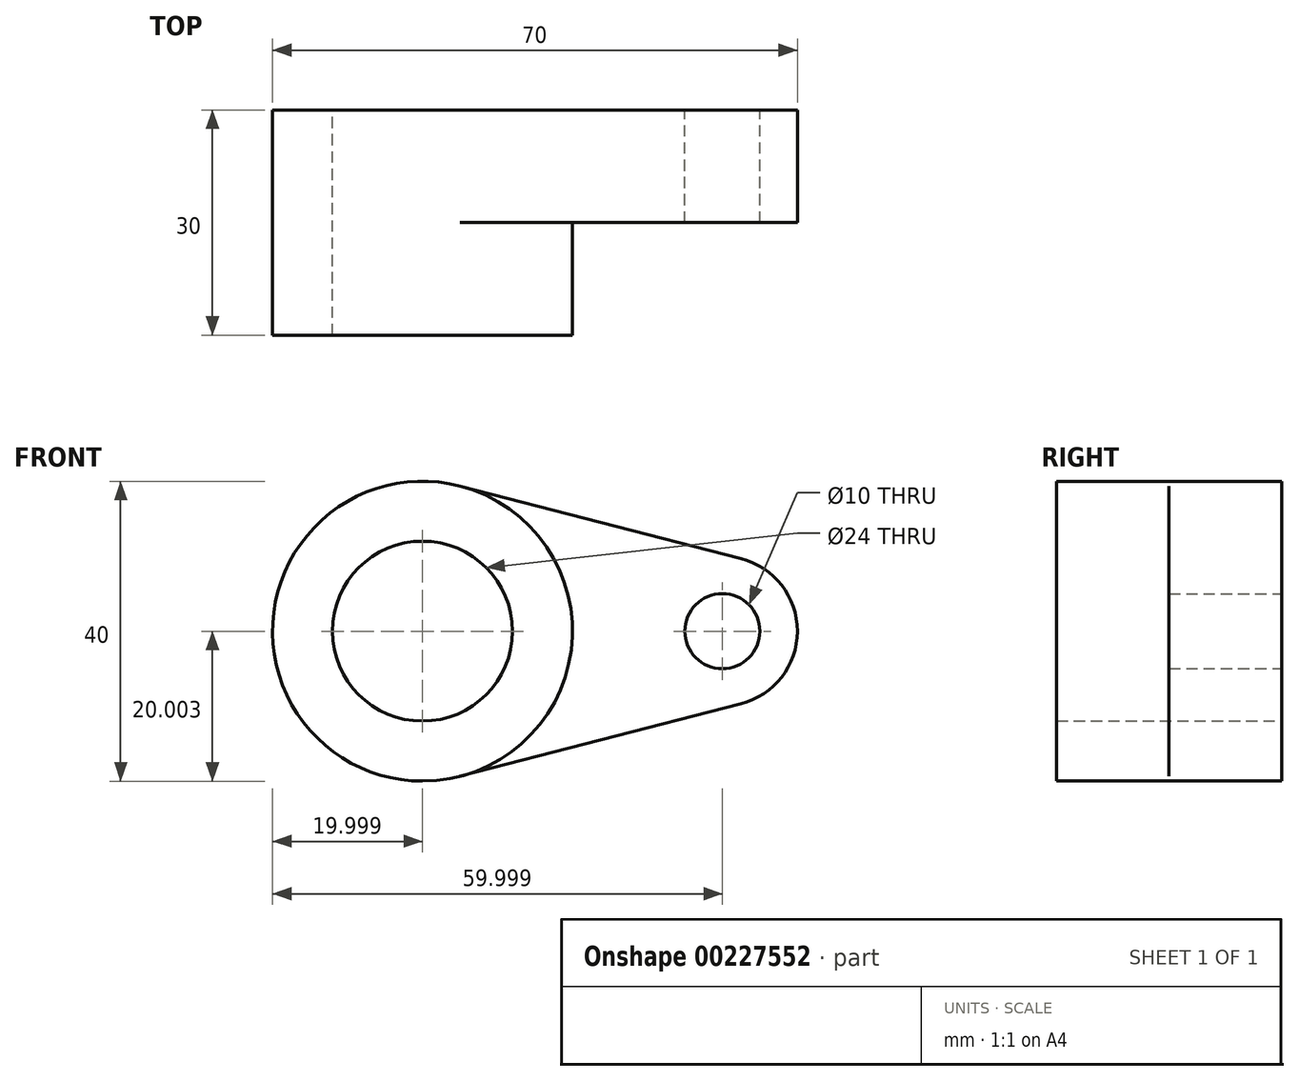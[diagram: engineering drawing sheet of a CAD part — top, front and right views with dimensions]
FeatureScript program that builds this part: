
annotation { "Feature Type Name" : "Feature", "Feature Type Description" : "" }
export const myFeature = defineFeature(function(context is Context, id is Id, definition is map)
    precondition{}
    {
        {
            var Q0;
            Q0=qCreatedBy(makeId("Front.planeOp"),FACE);
            var sketch = newSketch(context, id + "F0", { "sketchPlane" : qUnion([Q0])});
            skCircle(sketch, "E0", {"center": v(-20.94, 10.91) * mm, "radius": 20 * mm});
            skCircle(sketch, "E1", {"center": v(-20.94, 10.91) * mm, "radius": 12 * mm});
            skArc(sketch, "E2", {"start": v(21.56, 1.23) * mm, "mid": v(29.06, 10.91) * mm, "end": v(21.56, 20.6) * mm});
            skCircle(sketch, "E3", {"center": v(19.06, 10.91) * mm, "radius": 5 * mm});
            skLineSegment(sketch, "E4", {"start": v(-15.94, 30.28) * mm, "end": v(21.56, 20.6) * mm});
            skLineSegment(sketch, "E5", {"start": v(-15.94, -8.45) * mm, "end": v(21.56, 1.23) * mm});
            skSolve(sketch);
        }
        {
            var Q0;
            Q0=makeQuery(id+"F0.imprint","IMPRINT",FACE,{"disambiguationData":[TD([[makeQuery(id+"F0.imprint","IMPRINT",EDGE,{"derivedFrom":sQuery(id+"F0.wireOp",EDGE,"E2")}),1.0]])]});
            extrude(context, id + "F1", {"entities" : qUnion([Q0]), "depth" : 15 * mm});
        }
        {
            var Q0;
            Q0=makeQuery(id+"F0.imprint","IMPRINT",FACE,{"disambiguationData":[TD([[makeQuery(id+"F0.imprint","IMPRINT",EDGE,{"derivedFrom":sQuery(id+"F0.wireOp",EDGE,"E1")}),-1.0]])]});
            extrude(context, id + "F2", {"entities" : qUnion([Q0]), "operationType" : NewBodyOperationType.ADD, "depth" : 30 * mm});
        }
    });
